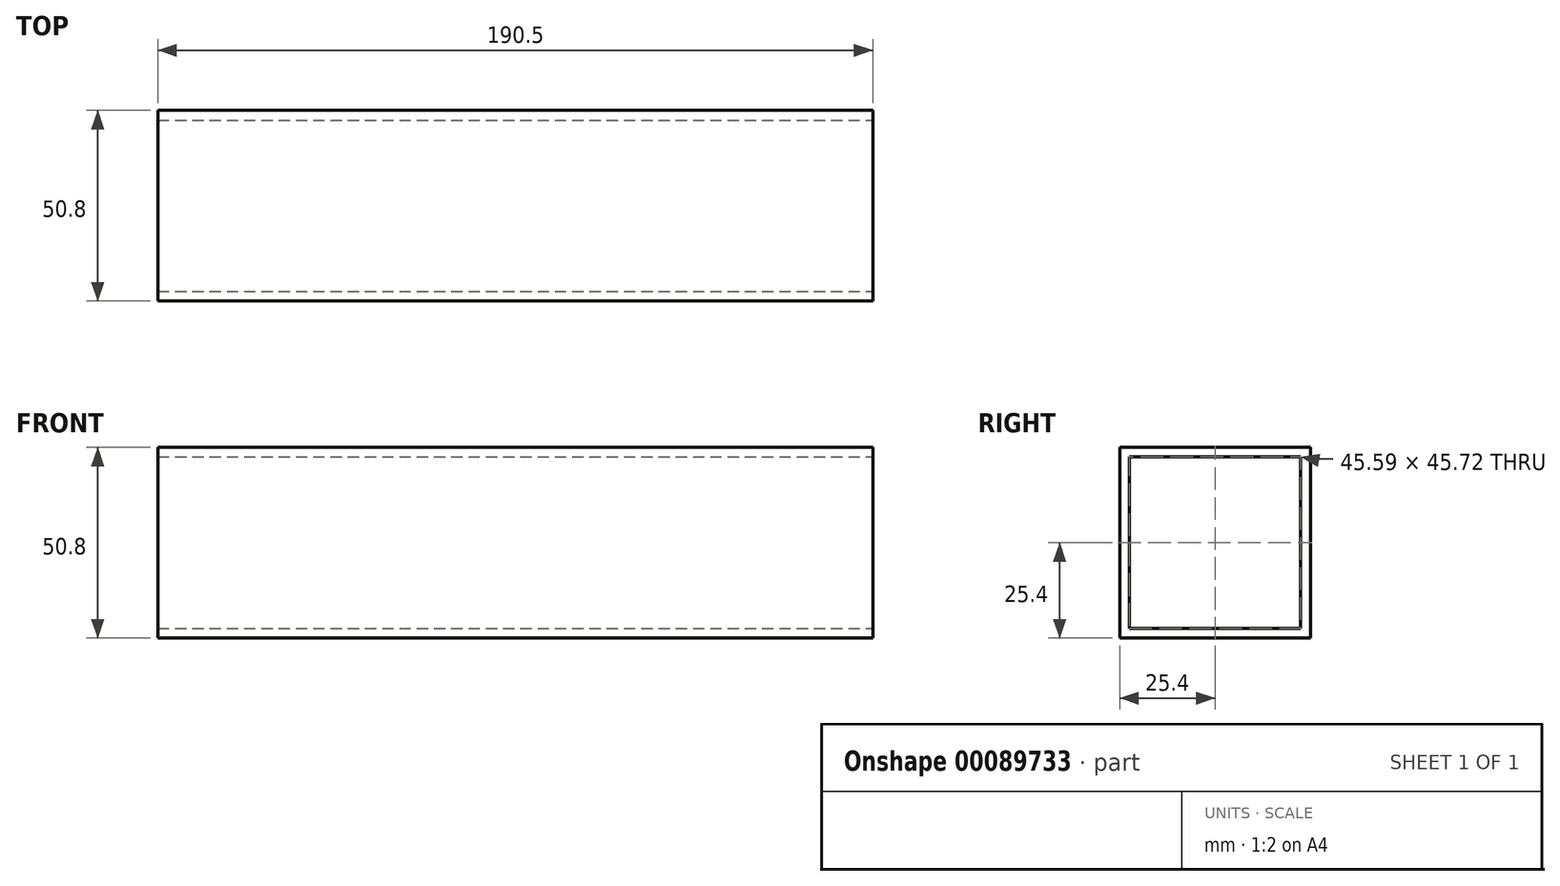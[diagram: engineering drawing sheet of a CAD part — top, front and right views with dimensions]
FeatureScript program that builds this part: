
annotation { "Feature Type Name" : "Feature", "Feature Type Description" : "" }
export const myFeature = defineFeature(function(context is Context, id is Id, definition is map)
    precondition{}
    {
        {
            var Q0;
            Q0=qCreatedBy(makeId("Top.planeOp"),FACE);
            var sketch = newSketch(context, id + "F0", { "sketchPlane" : qUnion([Q0])});
            skLineSegment(sketch, "E0.bottom", {"start": v(95.25, 25.4) * mm, "end": v(-95.25, 25.4) * mm});
            skLineSegment(sketch, "E0.top", {"start": v(95.25, -25.4) * mm, "end": v(-95.25, -25.4) * mm});
            skLineSegment(sketch, "E0.left", {"start": v(95.25, 25.4) * mm, "end": v(95.25, -25.4) * mm});
            skLineSegment(sketch, "E0.right", {"start": v(-95.25, 25.4) * mm, "end": v(-95.25, -25.4) * mm});
            skPoint(sketch, "E0.middle", {"position": v(0, 0) * mm});
            skSolve(sketch);
        }
        {
            var Q0;
            Q0=makeQuery(id+"F0.imprint","IMPRINT",FACE,{"disambiguationData":[TD([[makeQuery(id+"F0.imprint","IMPRINT",EDGE,{"derivedFrom":sQuery(id+"F0.wireOp",EDGE,"E0.bottom")}),1.0]])]});
            extrude(context, id + "F1", {"entities" : qUnion([Q0]), "depth" : 50.8 * mm});
        }
        {
            var Q0;
            Q0=makeQuery(id+"F1.opExtrude","SWEPT_FACE",FACE,{"disambiguationData":[OSD([sQuery(id+"F0.wireOp",EDGE,"E0.left")])]});
            var sketch = newSketch(context, id + "F2", { "sketchPlane" : qUnion([Q0])});
            skLineSegment(sketch, "E1.bottom", {"start": v(22.8, 48.26) * mm, "end": v(-22.8, 48.26) * mm});
            skLineSegment(sketch, "E1.top", {"start": v(22.8, 2.54) * mm, "end": v(-22.8, 2.54) * mm});
            skLineSegment(sketch, "E1.left", {"start": v(22.8, 48.26) * mm, "end": v(22.8, 2.54) * mm});
            skLineSegment(sketch, "E1.right", {"start": v(-22.8, 48.26) * mm, "end": v(-22.8, 2.54) * mm});
            skPoint(sketch, "E1.middle", {"position": v(0, 25.4) * mm});
            skPoint(sketch, "E1.middle.positionSnap0", {"position": v(-25.4, 25.4) * mm});
            skPoint(sketch, "E1.centerSnap0", {"position": v(-25.4, 25.4) * mm});
            skSolve(sketch);
        }
        {
            var Q0;
            Q0=makeQuery(id+"F2.imprint","IMPRINT",FACE,{"disambiguationData":[TD([[makeQuery(id+"F2.imprint","IMPRINT",EDGE,{"derivedFrom":sQuery(id+"F2.wireOp",EDGE,"E1.bottom")}),1.0]])]});
            extrude(context, id + "F3", {"entities" : qUnion([Q0]), "operationType" : NewBodyOperationType.REMOVE, "oppositeDirection" : true, "depth" : 237.57 * mm});
        }
    });
